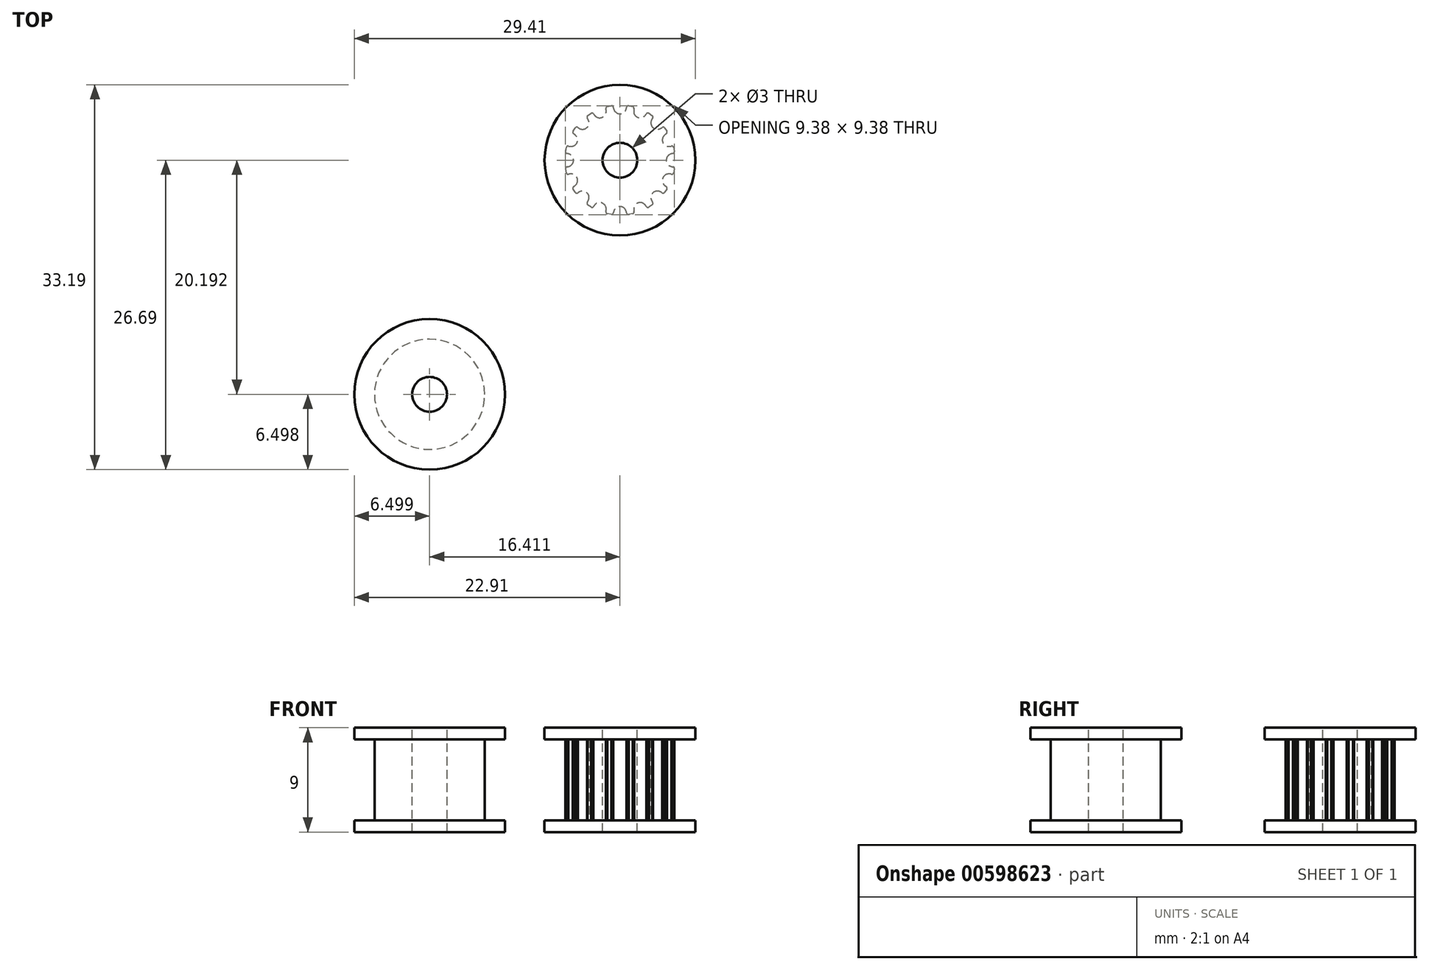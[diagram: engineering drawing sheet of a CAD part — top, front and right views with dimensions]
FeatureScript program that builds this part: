
annotation { "Feature Type Name" : "Feature", "Feature Type Description" : "" }
export const myFeature = defineFeature(function(context is Context, id is Id, definition is map)
    precondition{}
    {
        {
            var Q0;
            Q0=qCreatedBy(makeId("Top.planeOp"),FACE);
            var sketch = newSketch(context, id + "F0", { "sketchPlane" : qUnion([Q0])});
            skLineSegment(sketch, "E0", {"start": v(0, 0) * mm, "end": v(8.05, 0) * mm, "construction": true});
            skArc(sketch, "E1", {"start": v(4.75, 0) * mm, "mid": v(4.66, 0.93) * mm, "end": v(4.39, 1.82) * mm, "construction": true});
            skLineSegment(sketch, "E2", {"start": v(0, 0) * mm, "end": v(4.39, 1.82) * mm, "construction": true});
            skPoint(sketch, "E3", {"position": v(4, 0) * mm});
            skPoint(sketch, "E4", {"position": v(4.55, 0) * mm});
            skArc(sketch, "E5", {"start": v(4.33, 0.5) * mm, "mid": v(4, 0) * mm, "end": v(4.33, -0.5) * mm});
            skArc(sketch, "E6", {"start": v(4.56, 0.58) * mm, "mid": v(4.45, 0.55) * mm, "end": v(4.33, 0.5) * mm});
            skArc(sketch, "E7", {"start": v(4.6, 0) * mm, "mid": v(4.51, 0.9) * mm, "end": v(4.25, 1.76) * mm, "construction": true});
            skArc(sketch, "E8", {"start": v(4.56, 0.58) * mm, "mid": v(4.66, 0.64) * mm, "end": v(4.7, 0.75) * mm});
            skArc(sketch, "E9", {"start": v(4.64, -1.03) * mm, "mid": v(4.72, -0.52) * mm, "end": v(4.75, 0) * mm, "construction": true});
            skLineSegment(sketch, "E10", {"start": v(0, 0) * mm, "end": v(4.66, 0.93) * mm, "construction": true});
            skPoint(sketch, "E11", {"position": v(4.66, 0.93) * mm});
            skArc(sketch, "E12.MirrorCS", {"start": v(4.44, 1.21) * mm, "mid": v(4.55, 1.2) * mm, "end": v(4.62, 1.1) * mm});
            skArc(sketch, "E13.MirrorCS", {"start": v(4.44, 1.21) * mm, "mid": v(4.32, 1.2) * mm, "end": v(4.2, 1.19) * mm});
            skArc(sketch, "E14.MirrorCS", {"start": v(4.2, 1.19) * mm, "mid": v(3.7, 1.53) * mm, "end": v(3.8, 2.13) * mm});
            skLineSegment(sketch, "E15", {"start": v(4.62, 1.1) * mm, "end": v(4.7, 0.75) * mm});
            skArc(sketch, "E16.1.0", {"start": v(3.8, 2.13) * mm, "mid": v(3.7, 1.53) * mm, "end": v(4.2, 1.19) * mm});
            skArc(sketch, "E16.1.1", {"start": v(4, 2.28) * mm, "mid": v(3.9, 2.2) * mm, "end": v(3.8, 2.13) * mm});
            skArc(sketch, "E16.1.2", {"start": v(4, 2.28) * mm, "mid": v(4.06, 2.37) * mm, "end": v(4.05, 2.49) * mm});
            skLineSegment(sketch, "E16.1.3", {"start": v(3.85, 2.79) * mm, "end": v(4.05, 2.49) * mm});
            skArc(sketch, "E16.1.4", {"start": v(3.64, 2.82) * mm, "mid": v(3.75, 2.85) * mm, "end": v(3.85, 2.79) * mm});
            skArc(sketch, "E16.1.5", {"start": v(3.64, 2.82) * mm, "mid": v(3.53, 2.76) * mm, "end": v(3.42, 2.7) * mm});
            skArc(sketch, "E16.2.0", {"start": v(2.7, 3.42) * mm, "mid": v(2.83, 2.83) * mm, "end": v(3.42, 2.7) * mm});
            skArc(sketch, "E16.2.1", {"start": v(2.82, 3.64) * mm, "mid": v(2.76, 3.53) * mm, "end": v(2.7, 3.42) * mm});
            skArc(sketch, "E16.2.2", {"start": v(2.82, 3.64) * mm, "mid": v(2.85, 3.75) * mm, "end": v(2.79, 3.85) * mm});
            skLineSegment(sketch, "E16.2.3", {"start": v(2.49, 4.05) * mm, "end": v(2.79, 3.85) * mm});
            skArc(sketch, "E16.2.4", {"start": v(2.28, 4) * mm, "mid": v(2.37, 4.06) * mm, "end": v(2.49, 4.05) * mm});
            skArc(sketch, "E16.2.5", {"start": v(2.28, 4) * mm, "mid": v(2.2, 3.9) * mm, "end": v(2.13, 3.8) * mm});
            skArc(sketch, "E16.3.0", {"start": v(1.19, 4.2) * mm, "mid": v(1.53, 3.7) * mm, "end": v(2.13, 3.8) * mm});
            skArc(sketch, "E16.3.1", {"start": v(1.21, 4.44) * mm, "mid": v(1.2, 4.32) * mm, "end": v(1.19, 4.2) * mm});
            skArc(sketch, "E16.3.2", {"start": v(1.21, 4.44) * mm, "mid": v(1.2, 4.55) * mm, "end": v(1.1, 4.62) * mm});
            skLineSegment(sketch, "E16.3.3", {"start": v(0.75, 4.7) * mm, "end": v(1.1, 4.62) * mm});
            skArc(sketch, "E16.3.4", {"start": v(0.58, 4.56) * mm, "mid": v(0.64, 4.66) * mm, "end": v(0.75, 4.7) * mm});
            skArc(sketch, "E16.3.5", {"start": v(0.58, 4.56) * mm, "mid": v(0.55, 4.45) * mm, "end": v(0.5, 4.33) * mm});
            skArc(sketch, "E16.4.0", {"start": v(-0.5, 4.33) * mm, "mid": v(0, 4) * mm, "end": v(0.5, 4.33) * mm});
            skArc(sketch, "E16.4.1", {"start": v(-0.58, 4.56) * mm, "mid": v(-0.55, 4.45) * mm, "end": v(-0.5, 4.33) * mm});
            skArc(sketch, "E16.4.2", {"start": v(-0.58, 4.56) * mm, "mid": v(-0.64, 4.66) * mm, "end": v(-0.75, 4.7) * mm});
            skLineSegment(sketch, "E16.4.3", {"start": v(-1.1, 4.62) * mm, "end": v(-0.75, 4.7) * mm});
            skArc(sketch, "E16.4.4", {"start": v(-1.21, 4.44) * mm, "mid": v(-1.2, 4.55) * mm, "end": v(-1.1, 4.62) * mm});
            skArc(sketch, "E16.4.5", {"start": v(-1.21, 4.44) * mm, "mid": v(-1.2, 4.32) * mm, "end": v(-1.19, 4.2) * mm});
            skArc(sketch, "E16.5.0", {"start": v(-2.13, 3.8) * mm, "mid": v(-1.53, 3.7) * mm, "end": v(-1.19, 4.2) * mm});
            skArc(sketch, "E16.5.1", {"start": v(-2.28, 4) * mm, "mid": v(-2.2, 3.9) * mm, "end": v(-2.13, 3.8) * mm});
            skArc(sketch, "E16.5.2", {"start": v(-2.28, 4) * mm, "mid": v(-2.37, 4.06) * mm, "end": v(-2.49, 4.05) * mm});
            skLineSegment(sketch, "E16.5.3", {"start": v(-2.79, 3.85) * mm, "end": v(-2.49, 4.05) * mm});
            skArc(sketch, "E16.5.4", {"start": v(-2.82, 3.64) * mm, "mid": v(-2.85, 3.75) * mm, "end": v(-2.79, 3.85) * mm});
            skArc(sketch, "E16.5.5", {"start": v(-2.82, 3.64) * mm, "mid": v(-2.76, 3.53) * mm, "end": v(-2.7, 3.42) * mm});
            skArc(sketch, "E16.6.0", {"start": v(-3.42, 2.7) * mm, "mid": v(-2.83, 2.83) * mm, "end": v(-2.7, 3.42) * mm});
            skArc(sketch, "E16.6.1", {"start": v(-3.64, 2.82) * mm, "mid": v(-3.53, 2.76) * mm, "end": v(-3.42, 2.7) * mm});
            skArc(sketch, "E16.6.2", {"start": v(-3.64, 2.82) * mm, "mid": v(-3.75, 2.85) * mm, "end": v(-3.85, 2.79) * mm});
            skLineSegment(sketch, "E16.6.3", {"start": v(-4.05, 2.49) * mm, "end": v(-3.85, 2.79) * mm});
            skArc(sketch, "E16.6.4", {"start": v(-4, 2.28) * mm, "mid": v(-4.06, 2.37) * mm, "end": v(-4.05, 2.49) * mm});
            skArc(sketch, "E16.6.5", {"start": v(-4, 2.28) * mm, "mid": v(-3.9, 2.2) * mm, "end": v(-3.8, 2.13) * mm});
            skArc(sketch, "E16.7.0", {"start": v(-4.2, 1.19) * mm, "mid": v(-3.7, 1.53) * mm, "end": v(-3.8, 2.13) * mm});
            skArc(sketch, "E16.7.1", {"start": v(-4.44, 1.21) * mm, "mid": v(-4.32, 1.2) * mm, "end": v(-4.2, 1.19) * mm});
            skArc(sketch, "E16.7.2", {"start": v(-4.44, 1.21) * mm, "mid": v(-4.55, 1.2) * mm, "end": v(-4.62, 1.1) * mm});
            skLineSegment(sketch, "E16.7.3", {"start": v(-4.7, 0.75) * mm, "end": v(-4.62, 1.1) * mm});
            skArc(sketch, "E16.7.4", {"start": v(-4.56, 0.58) * mm, "mid": v(-4.66, 0.64) * mm, "end": v(-4.7, 0.75) * mm});
            skArc(sketch, "E16.7.5", {"start": v(-4.56, 0.58) * mm, "mid": v(-4.45, 0.55) * mm, "end": v(-4.33, 0.5) * mm});
            skArc(sketch, "E16.8.0", {"start": v(-4.33, -0.5) * mm, "mid": v(-4, 0) * mm, "end": v(-4.33, 0.5) * mm});
            skArc(sketch, "E16.8.1", {"start": v(-4.56, -0.58) * mm, "mid": v(-4.45, -0.55) * mm, "end": v(-4.33, -0.5) * mm});
            skArc(sketch, "E16.8.2", {"start": v(-4.56, -0.58) * mm, "mid": v(-4.66, -0.64) * mm, "end": v(-4.7, -0.75) * mm});
            skLineSegment(sketch, "E16.8.3", {"start": v(-4.62, -1.1) * mm, "end": v(-4.7, -0.75) * mm});
            skArc(sketch, "E16.8.4", {"start": v(-4.44, -1.21) * mm, "mid": v(-4.55, -1.2) * mm, "end": v(-4.62, -1.1) * mm});
            skArc(sketch, "E16.8.5", {"start": v(-4.44, -1.21) * mm, "mid": v(-4.32, -1.2) * mm, "end": v(-4.2, -1.19) * mm});
            skArc(sketch, "E16.9.0", {"start": v(-3.8, -2.13) * mm, "mid": v(-3.7, -1.53) * mm, "end": v(-4.2, -1.19) * mm});
            skArc(sketch, "E16.9.1", {"start": v(-4, -2.28) * mm, "mid": v(-3.9, -2.2) * mm, "end": v(-3.8, -2.13) * mm});
            skArc(sketch, "E16.9.2", {"start": v(-4, -2.28) * mm, "mid": v(-4.06, -2.37) * mm, "end": v(-4.05, -2.49) * mm});
            skLineSegment(sketch, "E16.9.3", {"start": v(-3.85, -2.79) * mm, "end": v(-4.05, -2.49) * mm});
            skArc(sketch, "E16.9.4", {"start": v(-3.64, -2.82) * mm, "mid": v(-3.75, -2.85) * mm, "end": v(-3.85, -2.79) * mm});
            skArc(sketch, "E16.9.5", {"start": v(-3.64, -2.82) * mm, "mid": v(-3.53, -2.76) * mm, "end": v(-3.42, -2.7) * mm});
            skArc(sketch, "E16.10.0", {"start": v(-2.7, -3.42) * mm, "mid": v(-2.83, -2.83) * mm, "end": v(-3.42, -2.7) * mm});
            skArc(sketch, "E16.10.1", {"start": v(-2.82, -3.64) * mm, "mid": v(-2.76, -3.53) * mm, "end": v(-2.7, -3.42) * mm});
            skArc(sketch, "E16.10.2", {"start": v(-2.82, -3.64) * mm, "mid": v(-2.85, -3.75) * mm, "end": v(-2.79, -3.85) * mm});
            skLineSegment(sketch, "E16.10.3", {"start": v(-2.49, -4.05) * mm, "end": v(-2.79, -3.85) * mm});
            skArc(sketch, "E16.10.4", {"start": v(-2.28, -4) * mm, "mid": v(-2.37, -4.06) * mm, "end": v(-2.49, -4.05) * mm});
            skArc(sketch, "E16.10.5", {"start": v(-2.28, -4) * mm, "mid": v(-2.2, -3.9) * mm, "end": v(-2.13, -3.8) * mm});
            skArc(sketch, "E16.11.0", {"start": v(-1.19, -4.2) * mm, "mid": v(-1.53, -3.7) * mm, "end": v(-2.13, -3.8) * mm});
            skArc(sketch, "E16.11.1", {"start": v(-1.21, -4.44) * mm, "mid": v(-1.2, -4.32) * mm, "end": v(-1.19, -4.2) * mm});
            skArc(sketch, "E16.11.2", {"start": v(-1.21, -4.44) * mm, "mid": v(-1.2, -4.55) * mm, "end": v(-1.1, -4.62) * mm});
            skLineSegment(sketch, "E16.11.3", {"start": v(-0.75, -4.7) * mm, "end": v(-1.1, -4.62) * mm});
            skArc(sketch, "E16.11.4", {"start": v(-0.58, -4.56) * mm, "mid": v(-0.64, -4.66) * mm, "end": v(-0.75, -4.7) * mm});
            skArc(sketch, "E16.11.5", {"start": v(-0.58, -4.56) * mm, "mid": v(-0.55, -4.45) * mm, "end": v(-0.5, -4.33) * mm});
            skArc(sketch, "E16.12.0", {"start": v(0.5, -4.33) * mm, "mid": v(0, -4) * mm, "end": v(-0.5, -4.33) * mm});
            skArc(sketch, "E16.12.1", {"start": v(0.58, -4.56) * mm, "mid": v(0.55, -4.45) * mm, "end": v(0.5, -4.33) * mm});
            skArc(sketch, "E16.12.2", {"start": v(0.58, -4.56) * mm, "mid": v(0.64, -4.66) * mm, "end": v(0.75, -4.7) * mm});
            skLineSegment(sketch, "E16.12.3", {"start": v(1.1, -4.62) * mm, "end": v(0.75, -4.7) * mm});
            skArc(sketch, "E16.12.4", {"start": v(1.21, -4.44) * mm, "mid": v(1.2, -4.55) * mm, "end": v(1.1, -4.62) * mm});
            skArc(sketch, "E16.12.5", {"start": v(1.21, -4.44) * mm, "mid": v(1.2, -4.32) * mm, "end": v(1.19, -4.2) * mm});
            skArc(sketch, "E16.13.0", {"start": v(2.13, -3.8) * mm, "mid": v(1.53, -3.7) * mm, "end": v(1.19, -4.2) * mm});
            skArc(sketch, "E16.13.1", {"start": v(2.28, -4) * mm, "mid": v(2.2, -3.9) * mm, "end": v(2.13, -3.8) * mm});
            skArc(sketch, "E16.13.2", {"start": v(2.28, -4) * mm, "mid": v(2.37, -4.06) * mm, "end": v(2.49, -4.05) * mm});
            skLineSegment(sketch, "E16.13.3", {"start": v(2.79, -3.85) * mm, "end": v(2.49, -4.05) * mm});
            skArc(sketch, "E16.13.4", {"start": v(2.82, -3.64) * mm, "mid": v(2.85, -3.75) * mm, "end": v(2.79, -3.85) * mm});
            skArc(sketch, "E16.13.5", {"start": v(2.82, -3.64) * mm, "mid": v(2.76, -3.53) * mm, "end": v(2.7, -3.42) * mm});
            skArc(sketch, "E16.14.0", {"start": v(3.42, -2.7) * mm, "mid": v(2.83, -2.83) * mm, "end": v(2.7, -3.42) * mm});
            skArc(sketch, "E16.14.1", {"start": v(3.64, -2.82) * mm, "mid": v(3.53, -2.76) * mm, "end": v(3.42, -2.7) * mm});
            skArc(sketch, "E16.14.2", {"start": v(3.64, -2.82) * mm, "mid": v(3.75, -2.85) * mm, "end": v(3.85, -2.79) * mm});
            skLineSegment(sketch, "E16.14.3", {"start": v(4.05, -2.49) * mm, "end": v(3.85, -2.79) * mm});
            skArc(sketch, "E16.14.4", {"start": v(4, -2.28) * mm, "mid": v(4.06, -2.37) * mm, "end": v(4.05, -2.49) * mm});
            skArc(sketch, "E16.14.5", {"start": v(4, -2.28) * mm, "mid": v(3.9, -2.2) * mm, "end": v(3.8, -2.13) * mm});
            skArc(sketch, "E16.15.0", {"start": v(4.2, -1.19) * mm, "mid": v(3.7, -1.53) * mm, "end": v(3.8, -2.13) * mm});
            skArc(sketch, "E16.15.1", {"start": v(4.44, -1.21) * mm, "mid": v(4.32, -1.2) * mm, "end": v(4.2, -1.19) * mm});
            skArc(sketch, "E16.15.2", {"start": v(4.44, -1.21) * mm, "mid": v(4.55, -1.2) * mm, "end": v(4.62, -1.1) * mm});
            skLineSegment(sketch, "E16.15.3", {"start": v(4.7, -0.75) * mm, "end": v(4.62, -1.1) * mm});
            skArc(sketch, "E16.15.4", {"start": v(4.56, -0.58) * mm, "mid": v(4.66, -0.64) * mm, "end": v(4.7, -0.75) * mm});
            skArc(sketch, "E16.15.5", {"start": v(4.56, -0.58) * mm, "mid": v(4.45, -0.55) * mm, "end": v(4.33, -0.5) * mm});
            skCircle(sketch, "E17", {"center": v(0, 0) * mm, "radius": 1.5 * mm});
            skCircle(sketch, "E18", {"center": v(0, 0) * mm, "radius": 6.5 * mm});
            skSolve(sketch);
        }
        {
            var Q0;
            Q0=makeQuery(id+"F0.imprint","IMPRINT",FACE,{"disambiguationData":[TD([[makeQuery(id+"F0.imprint","IMPRINT",EDGE,{"derivedFrom":sQuery(id+"F0.wireOp",EDGE,"E5")}),-1.0]])]});
            var Q1;
            Q1=makeQuery(id+"F0.imprint","IMPRINT",FACE,{"disambiguationData":[TD([[makeQuery(id+"F0.imprint","IMPRINT",EDGE,{"derivedFrom":sQuery(id+"F0.wireOp",EDGE,"E5")}),1.0]])]});
            extrude(context, id + "F1", {"entities" : qUnion([Q0, Q1]), "oppositeDirection" : true, "depth" : 1 * mm, "offsetDistance" : 25 * mm});
        }
        {
            var Q0;
            Q0=makeQuery(id+"F0.imprint","IMPRINT",FACE,{"disambiguationData":[TD([[makeQuery(id+"F0.imprint","IMPRINT",EDGE,{"derivedFrom":sQuery(id+"F0.wireOp",EDGE,"E5")}),-1.0]])]});
            extrude(context, id + "F2", {"entities" : qUnion([Q0]), "operationType" : NewBodyOperationType.ADD, "depth" : 7 * mm, "offsetDistance" : 25 * mm});
        }
        {
            var Q0;
            Q0=makeQuery(id+"F0.imprint","IMPRINT",FACE,{"disambiguationData":[TD([[makeQuery(id+"F0.imprint","IMPRINT",EDGE,{"derivedFrom":sQuery(id+"F0.wireOp",EDGE,"E5")}),1.0]])]});
            var Q1;
            Q1=makeQuery(id+"F0.imprint","IMPRINT",FACE,{"disambiguationData":[TD([[makeQuery(id+"F0.imprint","IMPRINT",EDGE,{"derivedFrom":sQuery(id+"F0.wireOp",EDGE,"E5")}),-1.0]])]});
            var Q2;
            Q2=makeQuery(id+"F2.opExtrude","CAP_FACE",FACE,{"disambiguationData":[OSD([sQuery(id+"F0.wireOp",EDGE,"E5"),sQuery(id+"F0.wireOp",EDGE,"E6"),sQuery(id+"F0.wireOp",EDGE,"E8"),sQuery(id+"F0.wireOp",EDGE,"E12.MirrorCS"),sQuery(id+"F0.wireOp",EDGE,"E13.MirrorCS"),sQuery(id+"F0.wireOp",EDGE,"E15"),sQuery(id+"F0.wireOp",EDGE,"E16.1.0"),sQuery(id+"F0.wireOp",EDGE,"E16.1.1"),sQuery(id+"F0.wireOp",EDGE,"E16.1.2"),sQuery(id+"F0.wireOp",EDGE,"E16.1.3"),sQuery(id+"F0.wireOp",EDGE,"E16.1.4"),sQuery(id+"F0.wireOp",EDGE,"E16.1.5"),sQuery(id+"F0.wireOp",EDGE,"E16.2.0"),sQuery(id+"F0.wireOp",EDGE,"E16.2.1"),sQuery(id+"F0.wireOp",EDGE,"E16.2.2"),sQuery(id+"F0.wireOp",EDGE,"E16.2.3"),sQuery(id+"F0.wireOp",EDGE,"E16.2.4"),sQuery(id+"F0.wireOp",EDGE,"E16.2.5"),sQuery(id+"F0.wireOp",EDGE,"E16.3.0"),sQuery(id+"F0.wireOp",EDGE,"E16.3.1"),sQuery(id+"F0.wireOp",EDGE,"E16.3.2"),sQuery(id+"F0.wireOp",EDGE,"E16.3.3"),sQuery(id+"F0.wireOp",EDGE,"E16.3.4"),sQuery(id+"F0.wireOp",EDGE,"E16.3.5"),sQuery(id+"F0.wireOp",EDGE,"E16.4.0"),sQuery(id+"F0.wireOp",EDGE,"E16.4.1"),sQuery(id+"F0.wireOp",EDGE,"E16.4.2"),sQuery(id+"F0.wireOp",EDGE,"E16.4.3"),sQuery(id+"F0.wireOp",EDGE,"E16.4.4"),sQuery(id+"F0.wireOp",EDGE,"E16.4.5"),sQuery(id+"F0.wireOp",EDGE,"E16.5.0"),sQuery(id+"F0.wireOp",EDGE,"E16.5.1"),sQuery(id+"F0.wireOp",EDGE,"E16.5.2"),sQuery(id+"F0.wireOp",EDGE,"E16.5.3"),sQuery(id+"F0.wireOp",EDGE,"E16.5.4"),sQuery(id+"F0.wireOp",EDGE,"E16.5.5"),sQuery(id+"F0.wireOp",EDGE,"E16.6.0"),sQuery(id+"F0.wireOp",EDGE,"E16.6.1"),sQuery(id+"F0.wireOp",EDGE,"E16.6.2"),sQuery(id+"F0.wireOp",EDGE,"E16.6.3"),sQuery(id+"F0.wireOp",EDGE,"E16.6.4"),sQuery(id+"F0.wireOp",EDGE,"E16.6.5"),sQuery(id+"F0.wireOp",EDGE,"E16.7.0"),sQuery(id+"F0.wireOp",EDGE,"E16.7.1"),sQuery(id+"F0.wireOp",EDGE,"E16.7.2"),sQuery(id+"F0.wireOp",EDGE,"E16.7.3"),sQuery(id+"F0.wireOp",EDGE,"E16.7.4"),sQuery(id+"F0.wireOp",EDGE,"E16.7.5"),sQuery(id+"F0.wireOp",EDGE,"E16.8.0"),sQuery(id+"F0.wireOp",EDGE,"E16.8.1"),sQuery(id+"F0.wireOp",EDGE,"E16.8.2"),sQuery(id+"F0.wireOp",EDGE,"E16.8.3"),sQuery(id+"F0.wireOp",EDGE,"E16.8.4"),sQuery(id+"F0.wireOp",EDGE,"E16.8.5"),sQuery(id+"F0.wireOp",EDGE,"E16.9.0"),sQuery(id+"F0.wireOp",EDGE,"E16.9.1"),sQuery(id+"F0.wireOp",EDGE,"E16.9.2"),sQuery(id+"F0.wireOp",EDGE,"E16.9.3"),sQuery(id+"F0.wireOp",EDGE,"E16.9.4"),sQuery(id+"F0.wireOp",EDGE,"E16.9.5"),sQuery(id+"F0.wireOp",EDGE,"E16.10.0"),sQuery(id+"F0.wireOp",EDGE,"E16.10.1"),sQuery(id+"F0.wireOp",EDGE,"E16.10.2"),sQuery(id+"F0.wireOp",EDGE,"E16.10.3"),sQuery(id+"F0.wireOp",EDGE,"E16.10.4"),sQuery(id+"F0.wireOp",EDGE,"E16.10.5"),sQuery(id+"F0.wireOp",EDGE,"E16.11.0"),sQuery(id+"F0.wireOp",EDGE,"E16.11.1"),sQuery(id+"F0.wireOp",EDGE,"E16.11.2"),sQuery(id+"F0.wireOp",EDGE,"E16.11.3"),sQuery(id+"F0.wireOp",EDGE,"E16.11.4"),sQuery(id+"F0.wireOp",EDGE,"E16.11.5"),sQuery(id+"F0.wireOp",EDGE,"E16.12.0"),sQuery(id+"F0.wireOp",EDGE,"E16.12.1"),sQuery(id+"F0.wireOp",EDGE,"E16.12.2"),sQuery(id+"F0.wireOp",EDGE,"E16.12.3"),sQuery(id+"F0.wireOp",EDGE,"E16.12.4"),sQuery(id+"F0.wireOp",EDGE,"E16.12.5"),sQuery(id+"F0.wireOp",EDGE,"E16.13.0"),sQuery(id+"F0.wireOp",EDGE,"E16.13.1"),sQuery(id+"F0.wireOp",EDGE,"E16.13.2"),sQuery(id+"F0.wireOp",EDGE,"E16.13.3"),sQuery(id+"F0.wireOp",EDGE,"E16.13.4"),sQuery(id+"F0.wireOp",EDGE,"E16.13.5"),sQuery(id+"F0.wireOp",EDGE,"E16.14.0"),sQuery(id+"F0.wireOp",EDGE,"E16.14.1"),sQuery(id+"F0.wireOp",EDGE,"E16.14.2"),sQuery(id+"F0.wireOp",EDGE,"E16.14.3"),sQuery(id+"F0.wireOp",EDGE,"E16.14.4"),sQuery(id+"F0.wireOp",EDGE,"E16.14.5"),sQuery(id+"F0.wireOp",EDGE,"E16.15.0"),sQuery(id+"F0.wireOp",EDGE,"E16.15.1"),sQuery(id+"F0.wireOp",EDGE,"E16.15.2"),sQuery(id+"F0.wireOp",EDGE,"E16.15.3"),sQuery(id+"F0.wireOp",EDGE,"E16.15.4"),sQuery(id+"F0.wireOp",EDGE,"E16.15.5"),sQuery(id+"F0.wireOp",EDGE,"E17")])],"isStart":false});
            var Q3;
            Q3=makeQuery(id+"F2.opExtrude","CAP_FACE",FACE,{"disambiguationData":[OSD([sQuery(id+"F0.wireOp",EDGE,"E5"),sQuery(id+"F0.wireOp",EDGE,"E6"),sQuery(id+"F0.wireOp",EDGE,"E8"),sQuery(id+"F0.wireOp",EDGE,"E12.MirrorCS"),sQuery(id+"F0.wireOp",EDGE,"E13.MirrorCS"),sQuery(id+"F0.wireOp",EDGE,"E15"),sQuery(id+"F0.wireOp",EDGE,"E16.1.0"),sQuery(id+"F0.wireOp",EDGE,"E16.1.1"),sQuery(id+"F0.wireOp",EDGE,"E16.1.2"),sQuery(id+"F0.wireOp",EDGE,"E16.1.3"),sQuery(id+"F0.wireOp",EDGE,"E16.1.4"),sQuery(id+"F0.wireOp",EDGE,"E16.1.5"),sQuery(id+"F0.wireOp",EDGE,"E16.2.0"),sQuery(id+"F0.wireOp",EDGE,"E16.2.1"),sQuery(id+"F0.wireOp",EDGE,"E16.2.2"),sQuery(id+"F0.wireOp",EDGE,"E16.2.3"),sQuery(id+"F0.wireOp",EDGE,"E16.2.4"),sQuery(id+"F0.wireOp",EDGE,"E16.2.5"),sQuery(id+"F0.wireOp",EDGE,"E16.3.0"),sQuery(id+"F0.wireOp",EDGE,"E16.3.1"),sQuery(id+"F0.wireOp",EDGE,"E16.3.2"),sQuery(id+"F0.wireOp",EDGE,"E16.3.3"),sQuery(id+"F0.wireOp",EDGE,"E16.3.4"),sQuery(id+"F0.wireOp",EDGE,"E16.3.5"),sQuery(id+"F0.wireOp",EDGE,"E16.4.0"),sQuery(id+"F0.wireOp",EDGE,"E16.4.1"),sQuery(id+"F0.wireOp",EDGE,"E16.4.2"),sQuery(id+"F0.wireOp",EDGE,"E16.4.3"),sQuery(id+"F0.wireOp",EDGE,"E16.4.4"),sQuery(id+"F0.wireOp",EDGE,"E16.4.5"),sQuery(id+"F0.wireOp",EDGE,"E16.5.0"),sQuery(id+"F0.wireOp",EDGE,"E16.5.1"),sQuery(id+"F0.wireOp",EDGE,"E16.5.2"),sQuery(id+"F0.wireOp",EDGE,"E16.5.3"),sQuery(id+"F0.wireOp",EDGE,"E16.5.4"),sQuery(id+"F0.wireOp",EDGE,"E16.5.5"),sQuery(id+"F0.wireOp",EDGE,"E16.6.0"),sQuery(id+"F0.wireOp",EDGE,"E16.6.1"),sQuery(id+"F0.wireOp",EDGE,"E16.6.2"),sQuery(id+"F0.wireOp",EDGE,"E16.6.3"),sQuery(id+"F0.wireOp",EDGE,"E16.6.4"),sQuery(id+"F0.wireOp",EDGE,"E16.6.5"),sQuery(id+"F0.wireOp",EDGE,"E16.7.0"),sQuery(id+"F0.wireOp",EDGE,"E16.7.1"),sQuery(id+"F0.wireOp",EDGE,"E16.7.2"),sQuery(id+"F0.wireOp",EDGE,"E16.7.3"),sQuery(id+"F0.wireOp",EDGE,"E16.7.4"),sQuery(id+"F0.wireOp",EDGE,"E16.7.5"),sQuery(id+"F0.wireOp",EDGE,"E16.8.0"),sQuery(id+"F0.wireOp",EDGE,"E16.8.1"),sQuery(id+"F0.wireOp",EDGE,"E16.8.2"),sQuery(id+"F0.wireOp",EDGE,"E16.8.3"),sQuery(id+"F0.wireOp",EDGE,"E16.8.4"),sQuery(id+"F0.wireOp",EDGE,"E16.8.5"),sQuery(id+"F0.wireOp",EDGE,"E16.9.0"),sQuery(id+"F0.wireOp",EDGE,"E16.9.1"),sQuery(id+"F0.wireOp",EDGE,"E16.9.2"),sQuery(id+"F0.wireOp",EDGE,"E16.9.3"),sQuery(id+"F0.wireOp",EDGE,"E16.9.4"),sQuery(id+"F0.wireOp",EDGE,"E16.9.5"),sQuery(id+"F0.wireOp",EDGE,"E16.10.0"),sQuery(id+"F0.wireOp",EDGE,"E16.10.1"),sQuery(id+"F0.wireOp",EDGE,"E16.10.2"),sQuery(id+"F0.wireOp",EDGE,"E16.10.3"),sQuery(id+"F0.wireOp",EDGE,"E16.10.4"),sQuery(id+"F0.wireOp",EDGE,"E16.10.5"),sQuery(id+"F0.wireOp",EDGE,"E16.11.0"),sQuery(id+"F0.wireOp",EDGE,"E16.11.1"),sQuery(id+"F0.wireOp",EDGE,"E16.11.2"),sQuery(id+"F0.wireOp",EDGE,"E16.11.3"),sQuery(id+"F0.wireOp",EDGE,"E16.11.4"),sQuery(id+"F0.wireOp",EDGE,"E16.11.5"),sQuery(id+"F0.wireOp",EDGE,"E16.12.0"),sQuery(id+"F0.wireOp",EDGE,"E16.12.1"),sQuery(id+"F0.wireOp",EDGE,"E16.12.2"),sQuery(id+"F0.wireOp",EDGE,"E16.12.3"),sQuery(id+"F0.wireOp",EDGE,"E16.12.4"),sQuery(id+"F0.wireOp",EDGE,"E16.12.5"),sQuery(id+"F0.wireOp",EDGE,"E16.13.0"),sQuery(id+"F0.wireOp",EDGE,"E16.13.1"),sQuery(id+"F0.wireOp",EDGE,"E16.13.2"),sQuery(id+"F0.wireOp",EDGE,"E16.13.3"),sQuery(id+"F0.wireOp",EDGE,"E16.13.4"),sQuery(id+"F0.wireOp",EDGE,"E16.13.5"),sQuery(id+"F0.wireOp",EDGE,"E16.14.0"),sQuery(id+"F0.wireOp",EDGE,"E16.14.1"),sQuery(id+"F0.wireOp",EDGE,"E16.14.2"),sQuery(id+"F0.wireOp",EDGE,"E16.14.3"),sQuery(id+"F0.wireOp",EDGE,"E16.14.4"),sQuery(id+"F0.wireOp",EDGE,"E16.14.5"),sQuery(id+"F0.wireOp",EDGE,"E16.15.0"),sQuery(id+"F0.wireOp",EDGE,"E16.15.1"),sQuery(id+"F0.wireOp",EDGE,"E16.15.2"),sQuery(id+"F0.wireOp",EDGE,"E16.15.3"),sQuery(id+"F0.wireOp",EDGE,"E16.15.4"),sQuery(id+"F0.wireOp",EDGE,"E16.15.5"),sQuery(id+"F0.wireOp",EDGE,"E17")])],"isStart":false});
            extrude(context, id + "F3", {"entities" : qUnion([Q0, Q1]), "operationType" : NewBodyOperationType.ADD, "endBoundEntityFace" : qUnion([Q2]), "depth" : 8 * mm, "hasSecondDirection" : true, "secondDirectionBound" : SecondDirectionBoundingType.UP_TO_SURFACE, "secondDirectionOppositeDirection" : false, "secondDirectionBoundEntityFace" : qUnion([Q3]), "secondDirectionDepth" : 8 * mm, "offsetDistance" : 25 * mm});
        }
        {
            var Q0;
            Q0=qCreatedBy(makeId("Top.planeOp"),FACE);
            var sketch = newSketch(context, id + "F4", { "sketchPlane" : qUnion([Q0])});
            skCircle(sketch, "E19", {"center": v(-16.41, -20.2) * mm, "radius": 4.75 * mm});
            skCircle(sketch, "E20", {"center": v(-16.41, -20.2) * mm, "radius": 6.5 * mm});
            skCircle(sketch, "E21", {"center": v(-16.41, -20.2) * mm, "radius": 1.5 * mm});
            skSolve(sketch);
        }
        {
            var Q0;
            Q0=makeQuery(id+"F4.imprint","IMPRINT",FACE,{"disambiguationData":[TD([[makeQuery(id+"F4.imprint","IMPRINT",EDGE,{"derivedFrom":sQuery(id+"F4.wireOp",EDGE,"E19")}),-1.0]])]});
            var Q1;
            Q1=makeQuery(id+"F4.imprint","IMPRINT",FACE,{"disambiguationData":[TD([[makeQuery(id+"F4.imprint","IMPRINT",EDGE,{"derivedFrom":sQuery(id+"F4.wireOp",EDGE,"E19")}),1.0]])]});
            extrude(context, id + "F5", {"entities" : qUnion([Q0, Q1]), "oppositeDirection" : true, "depth" : 1 * mm, "offsetDistance" : 25 * mm});
        }
        {
            var Q0;
            Q0=makeQuery(id+"F4.imprint","IMPRINT",FACE,{"disambiguationData":[TD([[makeQuery(id+"F4.imprint","IMPRINT",EDGE,{"derivedFrom":sQuery(id+"F4.wireOp",EDGE,"E19")}),1.0]])]});
            extrude(context, id + "F6", {"entities" : qUnion([Q0]), "operationType" : NewBodyOperationType.ADD, "depth" : 7 * mm, "offsetDistance" : 25 * mm});
        }
        {
            var Q0;
            Q0=makeQuery(id+"F4.imprint","IMPRINT",FACE,{"disambiguationData":[TD([[makeQuery(id+"F4.imprint","IMPRINT",EDGE,{"derivedFrom":sQuery(id+"F4.wireOp",EDGE,"E19")}),1.0]])]});
            var Q1;
            Q1=makeQuery(id+"F4.imprint","IMPRINT",FACE,{"disambiguationData":[TD([[makeQuery(id+"F4.imprint","IMPRINT",EDGE,{"derivedFrom":sQuery(id+"F4.wireOp",EDGE,"E19")}),-1.0]])]});
            var Q2;
            Q2=sQuery(id+"F4.wireOp",EDGE,"E20");
            var Q3;
            Q3=sQuery(id+"F4.wireOp",EDGE,"E21");
            var Q4;
            Q4=makeQuery(id+"F6.opExtrude","CAP_FACE",FACE,{"disambiguationData":[OSD([sQuery(id+"F4.wireOp",EDGE,"E19"),sQuery(id+"F4.wireOp",EDGE,"E21")])],"isStart":false});
            extrude(context, id + "F7", {"entities" : qUnion([Q0, Q1]), "operationType" : NewBodyOperationType.ADD, "surfaceEntities" : qUnion([Q2, Q3]), "depth" : 8 * mm, "offsetDistance" : 25 * mm, "hasSecondDirection" : true, "secondDirectionBound" : SecondDirectionBoundingType.UP_TO_SURFACE, "secondDirectionOppositeDirection" : false, "secondDirectionDepth" : 25 * mm, "secondDirectionBoundEntityFace" : qUnion([Q4])});
        }
    });
